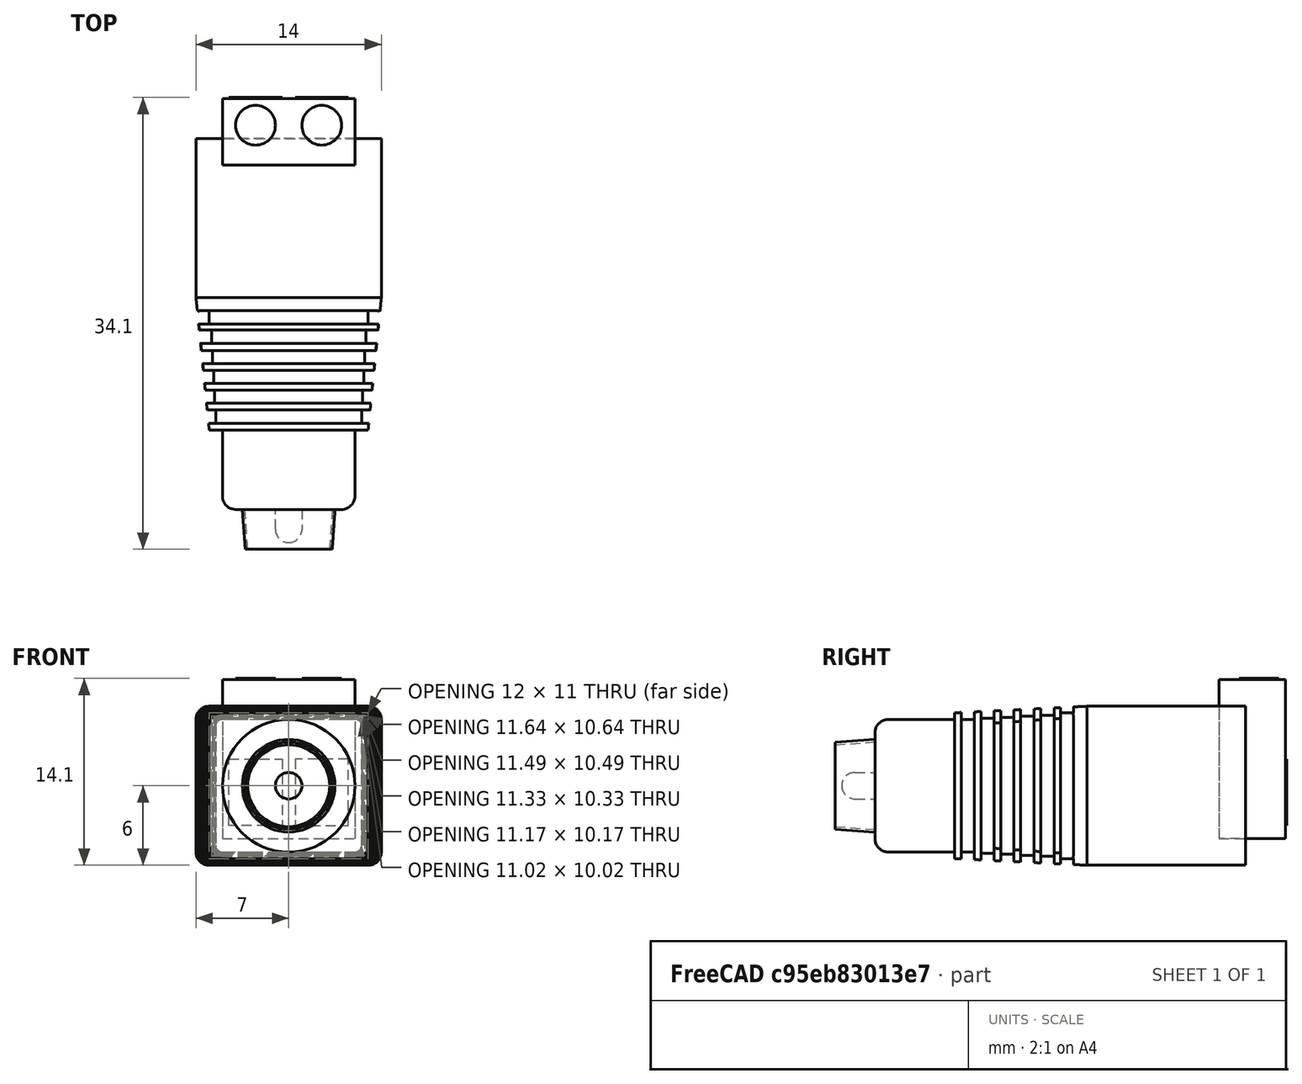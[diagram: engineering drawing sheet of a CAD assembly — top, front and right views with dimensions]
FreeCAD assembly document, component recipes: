
FREECAD ASSEMBLY — COMPONENT RECIPES ("dc_to_2wire")

This assembly document has 4 components, labeled P0..P3 below (a component is one placed body or linked part). 4 of them carry a construction recipe — the FreeCAD feature program that regenerates the part from scratch, quoted from this document or its linked companion documents; the rest are supplied as boundary geometry only. No exploded tour is included for this assembly.
COMPONENT P0 — recipe-attached ("aux001", modeled in this document).
Construction recipe (the document's own serialized feature program — sketch geometry with constraints, then the solid features built on it; lengths are millimeters unless a unit is written):

FEATURE [PartDesign::Plane] DatumPlane004
  AttachmentSupport = -> [SubtractivePipe]
  Length = 60
  MapMode = 5
  Placement = pos=(0,-28,0) rot=(1,0,0;1.5708rad)
  ResizeMode = 0
  Width = 60
FEATURE [Sketcher::SketchObject] Sketch009
  ArcFitTolerance = 1e-06
  AttachmentSupport = -> [DatumPlane004]
  ExternalTypes = [0]
  FullyConstrained = true
  MakeInternals = false
  MapMode = 5
  Placement = pos=(0,-28,0) rot=(1,0,0;1.5708rad)
  _ExternalGeoVersion = 1
  sketch-geometry (2):
    g0: Circle CenterX=0 CenterY=0 CenterZ=0 NormalX=0 NormalY=0 NormalZ=1 AngleXU=0 Radius=3.5
    g1: Circle CenterX=0 CenterY=0 CenterZ=0 NormalX=0 NormalY=0 NormalZ=1 AngleXU=0 Radius=3.3
  constraints (4):
    c: Diameter(g0) = 7
    c: Coincident(g0,g-1)
    c: Coincident(g1,g0)
    c: Distance(g1,g0) = 0.2
FEATURE [PartDesign::Pad] Pad007
  Direction = (0,-1,2e-16)
  Length = 3
  Length2 = 10
  Placement = pos=(0,-28,0) rot=(1,0,0;1.5708rad)
  Profile = -> Sketch009
  ReferenceAxis = -> Sketch009 [N_Axis]
  Refine = true
  SideType = 0
  Suppressed = false
  TaperAngle = -4
  Type = 0
  Type2 = 0
FEATURE [Sketcher::SketchObject] Sketch010
  ArcFitTolerance = 1e-06
  AttachmentSupport = -> [DatumPlane004]
  ExternalTypes = [0]
  FullyConstrained = true
  MakeInternals = false
  MapMode = 5
  Placement = pos=(0,-28,0) rot=(1,0,0;1.5708rad)
  _ExternalGeoVersion = 1
  sketch-geometry (1):
    g0: Circle CenterX=0 CenterY=0 CenterZ=0 NormalX=0 NormalY=0 NormalZ=1 AngleXU=0 Radius=1
  constraints (2):
    c: Diameter(g0) = 2
    c: Coincident(g0,g-1)
FEATURE [PartDesign::Pad] Pad008
  BaseFeature = -> Pad007
  Direction = (0,-1,2e-16)
  Length = 2.5
  Length2 = 10
  Placement = pos=(0,-28,0) rot=(1,0,0;1.5708rad)
  Profile = -> Sketch010
  ReferenceAxis = -> Sketch010 [N_Axis]
  Refine = true
  SideType = 0
  Suppressed = false
  Type = 0
  Type2 = 0
FEATURE [PartDesign::Fillet] Fillet001
  Base = -> Pad008 [Edge9]
  BaseFeature = -> Pad008
  Placement = pos=(0,-28,0) rot=(1,0,0;1.5708rad)
  Radius = 1
  Refine = true
  SupportTransform = false
  Suppressed = false
  UseAllEdges = false
FEATURE [PartDesign::Body] Body004  label="aux"
  AllowCompound = true
  Group = -> [DatumPlane004,Sketch009,Pad007,Sketch010,Pad008,Fillet001]
  Origin = -> Origin008
  Tip = -> Fillet001
COMPONENT P1 — recipe-attached ("base001", modeled in this document).
Construction recipe (the document's own serialized feature program — sketch geometry with constraints, then the solid features built on it; lengths are millimeters unless a unit is written):

FEATURE [Sketcher::SketchObject] Sketch
  ArcFitTolerance = 1e-06
  AttachmentSupport = -> [Origin]
  ExternalTypes = [0]
  FullyConstrained = true
  MakeInternals = false
  MapMode = 5
  Placement = pos=(0,0,0) rot=(1,0,0;1.5708rad)
  _ExternalGeoVersion = 1
  sketch-geometry (10):
    g0: LineSegment StartX=-6 StartY=-6 StartZ=0 EndX=6 EndY=-6 EndZ=0
    g1: LineSegment StartX=7 StartY=-5 StartZ=0 EndX=7 EndY=5 EndZ=0
    g2: LineSegment StartX=6 StartY=6 StartZ=0 EndX=-6 EndY=6 EndZ=0
    g3: LineSegment StartX=-7 StartY=5 StartZ=0 EndX=-7 EndY=-5 EndZ=0
    g4: ArcOfCircle CenterX=-6 CenterY=-5 CenterZ=0 NormalX=0 NormalY=0 NormalZ=1 AngleXU=0 Radius=1 StartAngle=3.14159 EndAngle=4.71239
    g5: ArcOfCircle CenterX=6 CenterY=-5 CenterZ=0 NormalX=0 NormalY=0 NormalZ=1 AngleXU=0 Radius=1 StartAngle=4.71239 EndAngle=6.28319
    g6: ArcOfCircle CenterX=6 CenterY=5 CenterZ=0 NormalX=0 NormalY=0 NormalZ=1 AngleXU=0 Radius=1 StartAngle=0 EndAngle=1.5708
    g7: ArcOfCircle CenterX=-6 CenterY=5 CenterZ=0 NormalX=0 NormalY=0 NormalZ=1 AngleXU=0 Radius=1 StartAngle=1.5708 EndAngle=3.14159
    g8: GeomPoint [constr] X=7 Y=6 Z=0
    g9: GeomPoint [constr] X=-2.33e-14 Y=2.6e-14 Z=0
  constraints (22):
    c: Tangent(g0,g4) = -1.5708
    c: Tangent(g0,g5) = -1.5708
    c: Tangent(g1,g5) = -1.5708
    c: Tangent(g1,g6) = -1.5708
    c: Tangent(g2,g6) = -1.5708
    c: Tangent(g2,g7) = -1.5708
    c: Tangent(g3,g7) = -1.5708
    c: Tangent(g3,g4) = -1.5708
    c: Horizontal(g0)
    c: Horizontal(g2)
    c: Vertical(g1)
    c: Vertical(g3)
    c: Equal(g4,g5)
    c: Equal(g5,g6)
    c: Equal(g6,g7)
    c: Symmetric(g2,g0,g9)
    c: PointOnObject(g8,g1)
    c: PointOnObject(g8,g2)
    c: Distance(g1,g3) = 14
    c: Distance(g0,g2) = 12
    c: Radius(g5) = 1
    c: Coincident(g9,g-1)
FEATURE [PartDesign::Pad] Pad
  Direction = (0,-1,2e-16)
  Length = 12
  Length2 = 10
  Profile = -> Sketch
  ReferenceAxis = -> Sketch [N_Axis]
  Refine = true
  SideType = 0
  Suppressed = false
  Type = 0
  Type2 = 0
FEATURE [PartDesign::Plane] DatumPlane
  AttachmentOffset = pos=(0,0,10) rot=(0,0,1;0rad)
  AttachmentSupport = -> [Pad]
  Length = 60
  MapMode = 5
  Placement = pos=(0,-22,2.2e-15) rot=(1,0,0;1.5708rad)
  ResizeMode = 0
  Width = 60
FEATURE [Sketcher::SketchObject] Sketch001
  ArcFitTolerance = 1e-06
  AttachmentSupport = -> [DatumPlane]
  ExternalTypes = [0]
  FullyConstrained = true
  MakeInternals = false
  MapMode = 5
  Placement = pos=(0,-22,2.2e-15) rot=(1,0,0;1.5708rad)
  _ExternalGeoVersion = 1
  sketch-geometry (10):
    g0: LineSegment StartX=-5 StartY=-5.5 StartZ=0 EndX=5 EndY=-5.5 EndZ=0
    g1: LineSegment StartX=6 StartY=-4.5 StartZ=0 EndX=6 EndY=4.5 EndZ=0
    g2: LineSegment StartX=5 StartY=5.5 StartZ=0 EndX=-5 EndY=5.5 EndZ=0
    g3: LineSegment StartX=-6 StartY=4.5 StartZ=0 EndX=-6 EndY=-4.5 EndZ=0
    g4: ArcOfCircle CenterX=-5 CenterY=-4.5 CenterZ=0 NormalX=0 NormalY=0 NormalZ=1 AngleXU=0 Radius=1 StartAngle=3.14159 EndAngle=4.71239
    g5: ArcOfCircle CenterX=5 CenterY=-4.5 CenterZ=0 NormalX=0 NormalY=0 NormalZ=1 AngleXU=0 Radius=1 StartAngle=4.71239 EndAngle=6.28319
    g6: ArcOfCircle CenterX=5 CenterY=4.5 CenterZ=0 NormalX=0 NormalY=0 NormalZ=1 AngleXU=0 Radius=1 StartAngle=0 EndAngle=1.5708
    g7: ArcOfCircle CenterX=-5 CenterY=4.5 CenterZ=0 NormalX=0 NormalY=0 NormalZ=1 AngleXU=0 Radius=1 StartAngle=1.5708 EndAngle=3.14159
    g8: GeomPoint [constr] X=6 Y=5.5 Z=0
    g9: GeomPoint [constr] X=0 Y=1.17e-14 Z=0
  constraints (22):
    c: Tangent(g0,g4) = -1.5708
    c: Tangent(g0,g5) = -1.5708
    c: Tangent(g1,g5) = -1.5708
    c: Tangent(g1,g6) = -1.5708
    c: Tangent(g2,g6) = -1.5708
    c: Tangent(g2,g7) = -1.5708
    c: Tangent(g3,g7) = -1.5708
    c: Tangent(g3,g4) = -1.5708
    c: Horizontal(g0)
    c: Horizontal(g2)
    c: Vertical(g1)
    c: Vertical(g3)
    c: Equal(g4,g5)
    c: Equal(g5,g6)
    c: Equal(g6,g7)
    c: Symmetric(g2,g0,g9)
    c: PointOnObject(g8,g1)
    c: PointOnObject(g8,g2)
    c: Distance(g1,g3) = 12
    c: Distance(g0,g2) = 11
    c: Radius(g5) = 1
    c: Coincident(g9,g-1)
FEATURE [PartDesign::AdditiveLoft] AdditiveLoft
  BaseFeature = -> Pad
  Closed = false
  Profile = -> Pad [Face10]
  Refine = true
  Ruled = false
  Sections = -> [Sketch001]
  Suppressed = false
FEATURE [Sketcher::SketchObject] Sketch002
  ArcFitTolerance = 1e-06
  AttachmentSupport = -> [AdditiveLoft]
  ExternalTypes = [0]
  FullyConstrained = true
  MakeInternals = false
  MapMode = 5
  Placement = pos=(0,-22,0) rot=(1,0,0;1.5708rad)
  _ExternalGeoVersion = 1
  sketch-geometry (1):
    g0: Circle CenterX=0 CenterY=0 CenterZ=0 NormalX=0 NormalY=0 NormalZ=1 AngleXU=0 Radius=5
  constraints (2):
    c: Diameter(g0) = 10
    c: Coincident(g0,g-1)
FEATURE [PartDesign::Pad] Pad001
  BaseFeature = -> AdditiveLoft
  Direction = (0,-1,2e-16)
  Length = 6
  Length2 = 10
  Profile = -> Sketch002
  ReferenceAxis = -> Sketch002 [N_Axis]
  Refine = true
  SideType = 0
  Suppressed = false
  Type = 0
  Type2 = 0
FEATURE [PartDesign::Fillet] Fillet
  Base = -> Pad001 [Edge55]
  BaseFeature = -> Pad001
  Radius = 1
  Refine = true
  SupportTransform = false
  Suppressed = false
  UseAllEdges = false
FEATURE [Sketcher::SketchObject] Sketch003
  ArcFitTolerance = 1e-06
  AttachmentSupport = -> [Origin]
  ExternalGeometry = -> [Fillet]
  ExternalTypes = [0]
  FullyConstrained = false
  MakeInternals = false
  MapMode = 5
  Placement = pos=(0,0,0) rot=(0.57735,0.57735,0.57735;2.0944rad)
  _ExternalGeoVersion = 1
  sketch-geometry (24):
    g0: LineSegment StartX=-13 StartY=6.5 StartZ=0 EndX=-14 EndY=6.5 EndZ=0
    g1: LineSegment StartX=-14 StartY=6.5 StartZ=0 EndX=-14 EndY=5.5 EndZ=0
    g2: LineSegment StartX=-14 StartY=5.5 StartZ=0 EndX=-13 EndY=5.5 EndZ=0
    g3: LineSegment StartX=-13 StartY=5.5 StartZ=0 EndX=-13 EndY=6.5 EndZ=0
    g4: LineSegment StartX=-14.4641 StartY=6.45747 StartZ=0 EndX=-15.4641 EndY=6.45747 EndZ=0
    g5: LineSegment StartX=-15.4641 StartY=6.45747 StartZ=0 EndX=-15.4641 EndY=5.3215 EndZ=0
    g6: LineSegment StartX=-15.4641 StartY=5.3215 StartZ=0 EndX=-14.4641 EndY=5.3215 EndZ=0
    g7: LineSegment StartX=-14.4641 StartY=5.3215 StartZ=0 EndX=-14.4641 EndY=6.45747 EndZ=0
    g8: LineSegment StartX=-15.9959 StartY=6.24299 StartZ=0 EndX=-16.9959 EndY=6.24299 EndZ=0
    g9: LineSegment StartX=-16.9959 StartY=6.24299 StartZ=0 EndX=-16.9959 EndY=5.24299 EndZ=0
    g10: LineSegment StartX=-16.9959 StartY=5.24299 StartZ=0 EndX=-15.9959 EndY=5.24299 EndZ=0
    g11: LineSegment StartX=-15.9959 StartY=5.24299 StartZ=0 EndX=-15.9959 EndY=6.24299 EndZ=0
    g12: LineSegment StartX=-17.4938 StartY=6.16449 StartZ=0 EndX=-18.4938 EndY=6.16449 EndZ=0
    g13: LineSegment StartX=-18.4938 StartY=6.16449 StartZ=0 EndX=-18.4938 EndY=5.16449 EndZ=0
    g14: LineSegment StartX=-18.4938 StartY=5.16449 StartZ=0 EndX=-17.4938 EndY=5.16449 EndZ=0
    g15: LineSegment StartX=-17.4938 StartY=5.16449 StartZ=0 EndX=-17.4938 EndY=6.16449 EndZ=0
    g16: LineSegment StartX=-18.9918 StartY=6.08598 StartZ=0 EndX=-19.9918 EndY=6.08598 EndZ=0
    g17: LineSegment StartX=-19.9918 StartY=6.08598 StartZ=0 EndX=-19.9918 EndY=5.08598 EndZ=0
    g18: LineSegment StartX=-19.9918 StartY=5.08598 StartZ=0 EndX=-18.9918 EndY=5.08598 EndZ=0
    g19: LineSegment StartX=-18.9918 StartY=5.08598 StartZ=0 EndX=-18.9918 EndY=6.08598 EndZ=0
    g20: LineSegment StartX=-20.4897 StartY=6.00748 StartZ=0 EndX=-21.4897 EndY=6.00748 EndZ=0
    g21: LineSegment StartX=-21.4897 StartY=6.00748 StartZ=0 EndX=-21.4897 EndY=5.00748 EndZ=0
    g22: LineSegment StartX=-21.4897 StartY=5.00748 StartZ=0 EndX=-20.4897 EndY=5.00748 EndZ=0
    g23: LineSegment StartX=-20.4897 StartY=5.00748 StartZ=0 EndX=-20.4897 EndY=6.00748 EndZ=0
  constraints (52):
    c: Coincident(g0,g1)
    c: Coincident(g1,g2)
    c: Coincident(g2,g3)
    c: Coincident(g3,g0)
    c: Horizontal(g0)
    c: Horizontal(g2)
    c: Vertical(g1)
    c: Vertical(g3)
    c: Distance(g1,g3) = 1
    c: Distance(g0,g2) = 1
    c: Distance(g-3,g3) = 1
    c: DistanceY(g-3,g0) = 0.5
    c: Coincident(g4,g5)
    c: Coincident(g8,g9)
    c: Coincident(g12,g13)
    c: Coincident(g16,g17)
    c: Coincident(g20,g21)
    c: Coincident(g5,g6)
    c: Coincident(g9,g10)
    c: Coincident(g13,g14)
    c: Coincident(g17,g18)
    c: Coincident(g21,g22)
    c: Coincident(g6,g7)
    c: Coincident(g10,g11)
    c: Coincident(g14,g15)
    c: Coincident(g18,g19)
    c: Coincident(g22,g23)
    c: Coincident(g7,g4)
    c: Coincident(g11,g8)
    c: Coincident(g15,g12)
    c: Coincident(g19,g16)
    c: Coincident(g23,g20)
    c: Horizontal(g4)
    c: Horizontal(g8)
    c: Horizontal(g12)
    c: Horizontal(g16)
    c: Horizontal(g20)
    c: Horizontal(g6)
    c: Horizontal(g10)
    c: Horizontal(g14)
    c: Horizontal(g18)
    c: Horizontal(g22)
    c: Vertical(g5)
    c: Vertical(g9)
    c: Vertical(g13)
    c: Vertical(g17)
    c: Vertical(g21)
    c: Vertical(g7)
    c: Vertical(g11)
    c: Vertical(g15)
    c: Vertical(g19)
    c: Vertical(g23)
FEATURE [PartDesign::SubtractivePipe] SubtractivePipe
  AuxiliaryCurvilinear = true
  AuxiliarySpineTangent = false
  BaseFeature = -> Fillet
  Binormal = (0,0,0)
  Mode = 0
  Profile = -> Sketch003
  Refine = true
  Spine = -> Fillet [Edge17,Edge16,Edge14,Edge12,Edge10,Edge8,Edge6,Edge7,Edge9,Edge11,Edge13,Edge15]
  SpineTangent = false
  Suppressed = false
  Transformation = 0
  Transition = 0
FEATURE [PartDesign::Body] Body  label="base"
  AllowCompound = true
  Group = -> [Sketch,Pad,DatumPlane,Sketch001,AdditiveLoft,Sketch002,Pad001,Fillet,Sketch003,SubtractivePipe]
  Origin = -> Origin
  Tip = -> SubtractivePipe
COMPONENT P2 — recipe-attached ("connectors001", modeled in this document).
Construction recipe (the document's own serialized feature program — sketch geometry with constraints, then the solid features built on it; lengths are millimeters unless a unit is written):

FEATURE [PartDesign::Plane] DatumPlane002
  AttachmentSupport = -> [Pad004]
  Length = 60
  MapMode = 5
  Placement = pos=(0,3,6) rot=(0,0.707107,0.707107;3.14159rad)
  ResizeMode = 0
  Width = 60
FEATURE [Sketcher::SketchObject] Sketch007
  ArcFitTolerance = 1e-06
  AttachmentSupport = -> [DatumPlane002]
  ExternalTypes = [0]
  FullyConstrained = true
  MakeInternals = false
  MapMode = 5
  Placement = pos=(0,3,6) rot=(0,0.707107,0.707107;3.14159rad)
  _ExternalGeoVersion = 1
  sketch-geometry (4):
    g0: LineSegment StartX=0.5 StartY=-4 StartZ=0 EndX=0.5 EndY=-9 EndZ=0
    g1: LineSegment StartX=0.5 StartY=-9 StartZ=0 EndX=4.5 EndY=-9 EndZ=0
    g2: LineSegment StartX=4.5 StartY=-9 StartZ=0 EndX=4.5 EndY=-4 EndZ=0
    g3: LineSegment StartX=4.5 StartY=-4 StartZ=0 EndX=0.5 EndY=-4 EndZ=0
  constraints (12):
    c: Coincident(g0,g1)
    c: Coincident(g1,g2)
    c: Coincident(g2,g3)
    c: Coincident(g3,g0)
    c: Vertical(g0)
    c: Vertical(g2)
    c: Horizontal(g1)
    c: Horizontal(g3)
    c: Distance(g0,g2) = 4
    c: Distance(g1,g3) = 5
    c: Distance(g-2,g0) = 0.5
    c: Distance(g-1,g3) = 4
FEATURE [PartDesign::Pad] Pad005
  Direction = (0,1,-2e-16)
  Length = 0.1
  Length2 = 10
  Placement = pos=(0,3,6) rot=(0,0.707107,0.707107;3.14159rad)
  Profile = -> Sketch007
  ReferenceAxis = -> Sketch007 [N_Axis]
  Refine = true
  SideType = 0
  Suppressed = false
  Type = 0
  Type2 = 0
FEATURE [PartDesign::Mirrored] Mirrored
  BaseFeature = -> Pad005
  MirrorPlane = -> Sketch007 [V_Axis]
  Originals = -> [Pad005]
  Placement = pos=(0,3,6) rot=(0,0.707107,0.707107;3.14159rad)
  Refine = true
  Suppressed = false
  TransformMode = 0
FEATURE [PartDesign::Plane] DatumPlane003
  AttachmentSupport = -> [Pad004]
  Length = 60
  MapMode = 5
  Placement = pos=(0,1.3e-15,8) rot=(0,0,1;0rad)
  ResizeMode = 0
  Width = 60
FEATURE [Sketcher::SketchObject] Sketch008
  ArcFitTolerance = 1e-06
  AttachmentSupport = -> [DatumPlane003]
  ExternalTypes = [0]
  FullyConstrained = true
  MakeInternals = false
  MapMode = 5
  Placement = pos=(0,1.3e-15,8) rot=(0,0,1;0rad)
  _ExternalGeoVersion = 1
  sketch-geometry (1):
    g0: Circle CenterX=-2.5 CenterY=1 CenterZ=0 NormalX=0 NormalY=0 NormalZ=1 AngleXU=0 Radius=1.5
  constraints (3):
    c: Diameter(g0) = 3
    c: Distance(g0,g-2) = 1
    c: Distance(g0,g-1) = 1
FEATURE [PartDesign::Pad] Pad006
  BaseFeature = -> Mirrored
  Direction = (0,0,1)
  Length = 0.1
  Length2 = 10
  Placement = pos=(0,3,6) rot=(0,0.707107,0.707107;3.14159rad)
  Profile = -> Sketch008
  ReferenceAxis = -> Sketch008 [N_Axis]
  Refine = true
  SideType = 0
  Suppressed = false
  Type = 0
  Type2 = 0
FEATURE [PartDesign::Mirrored] Mirrored001
  BaseFeature = -> Pad006
  MirrorPlane = -> Sketch008 [V_Axis]
  Originals = -> [Pad006]
  Placement = pos=(0,3,6) rot=(0,0.707107,0.707107;3.14159rad)
  Refine = true
  Suppressed = false
  TransformMode = 0
FEATURE [PartDesign::Body] Body003  label="connectors"
  AllowCompound = true
  Group = -> [DatumPlane002,Sketch007,Pad005,Mirrored,DatumPlane003,Sketch008,Pad006,Mirrored001]
  Origin = -> Origin006
  Tip = -> Mirrored001
COMPONENT P3 — recipe-attached ("sockets001", modeled in this document).
Construction recipe (the document's own serialized feature program — sketch geometry with constraints, then the solid features built on it; lengths are millimeters unless a unit is written):

FEATURE [PartDesign::Plane] DatumPlane001
  Length = 60
  MapMode = 5
  Placement = pos=(0,1.3e-15,6) rot=(0,0,1;0rad)
  ResizeMode = 0
  Width = 60
FEATURE [Sketcher::SketchObject] Sketch006
  ArcFitTolerance = 1e-06
  AttachmentSupport = -> [DatumPlane001]
  ExternalTypes = [0]
  FullyConstrained = true
  MakeInternals = false
  MapMode = 5
  Placement = pos=(0,1.3e-15,6) rot=(0,0,1;0rad)
  _ExternalGeoVersion = 1
  sketch-geometry (5):
    g0: LineSegment StartX=-5 StartY=-2 StartZ=0 EndX=5 EndY=-2 EndZ=0
    g1: LineSegment StartX=5 StartY=-2 StartZ=0 EndX=5 EndY=3 EndZ=0
    g2: LineSegment StartX=5 StartY=3 StartZ=0 EndX=-5 EndY=3 EndZ=0
    g3: LineSegment StartX=-5 StartY=3 StartZ=0 EndX=-5 EndY=-2 EndZ=0
    g4: GeomPoint [constr] X=0 Y=0.5 Z=0
  constraints (13):
    c: Coincident(g0,g1)
    c: Coincident(g1,g2)
    c: Coincident(g2,g3)
    c: Coincident(g3,g0)
    c: Horizontal(g0)
    c: Horizontal(g2)
    c: Vertical(g1)
    c: Vertical(g3)
    c: Symmetric(g2,g0,g4)
    c: Distance(g1,g3) = 10
    c: Distance(g0,g2) = 5
    c: PointOnObject(g4,g-2)
    c: Distance(g-1,g0) = 2
FEATURE [PartDesign::Pad] Pad004
  Direction = (0,0,1)
  Length = 2
  Length2 = 10
  Placement = pos=(0,1.3e-15,6) rot=(0,0,1;0rad)
  Profile = -> Sketch006
  ReferenceAxis = -> Sketch006 [N_Axis]
  Refine = true
  SideType = 1
  Suppressed = false
  Type = 0
  Type2 = 0
FEATURE [PartDesign::Body] Body002  label="sockets"
  AllowCompound = true
  Group = -> [DatumPlane001,Sketch006,Pad004]
  Origin = -> Origin004
  Tip = -> Pad004
PROVENANCE & LICENSES
A FreeCAD (.FCStd) document from a public repository crawl; recipes are the document's own serialized feature recipes (and, for linked parts, companion documents' recipes).
License: as declared in the source repository (recorded in the dataset sidecar).
